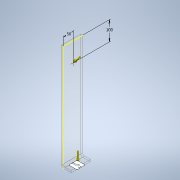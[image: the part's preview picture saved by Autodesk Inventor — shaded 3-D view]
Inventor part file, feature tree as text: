
AUTODESK INVENTOR PART (.ipt)
format: ipt  version: 2020 (Build 240168000, 168)  size: 144,896 bytes
history: native  units: in
note: dims shown in document units (in); Inventor stores cm internally (conversion verified against a paired STEP export)
features: sketch x2, extrude x1, fillet x1
ambient origin geometry x8: Origin, YZ Plane, XZ Plane, XY Plane, X Axis, Y Axis, Z Axis, Center Point
bodies: Solid1 (feature_tree)
feature tree (4):
  extrude  "Extrusion1"  Depth=1.9685in
  fillet  "Fillet1"  Radius=0.3937in
  sketch  "Sketch2"  dims[d4=0.3937in d5=3.937in d6=0.0in d7=0.3937in d8=1.9685in d9=3.937in]
  sketch  "Sketch1"  dims[d1=21.6535in d2=1.9685in d3=0.3937in]
